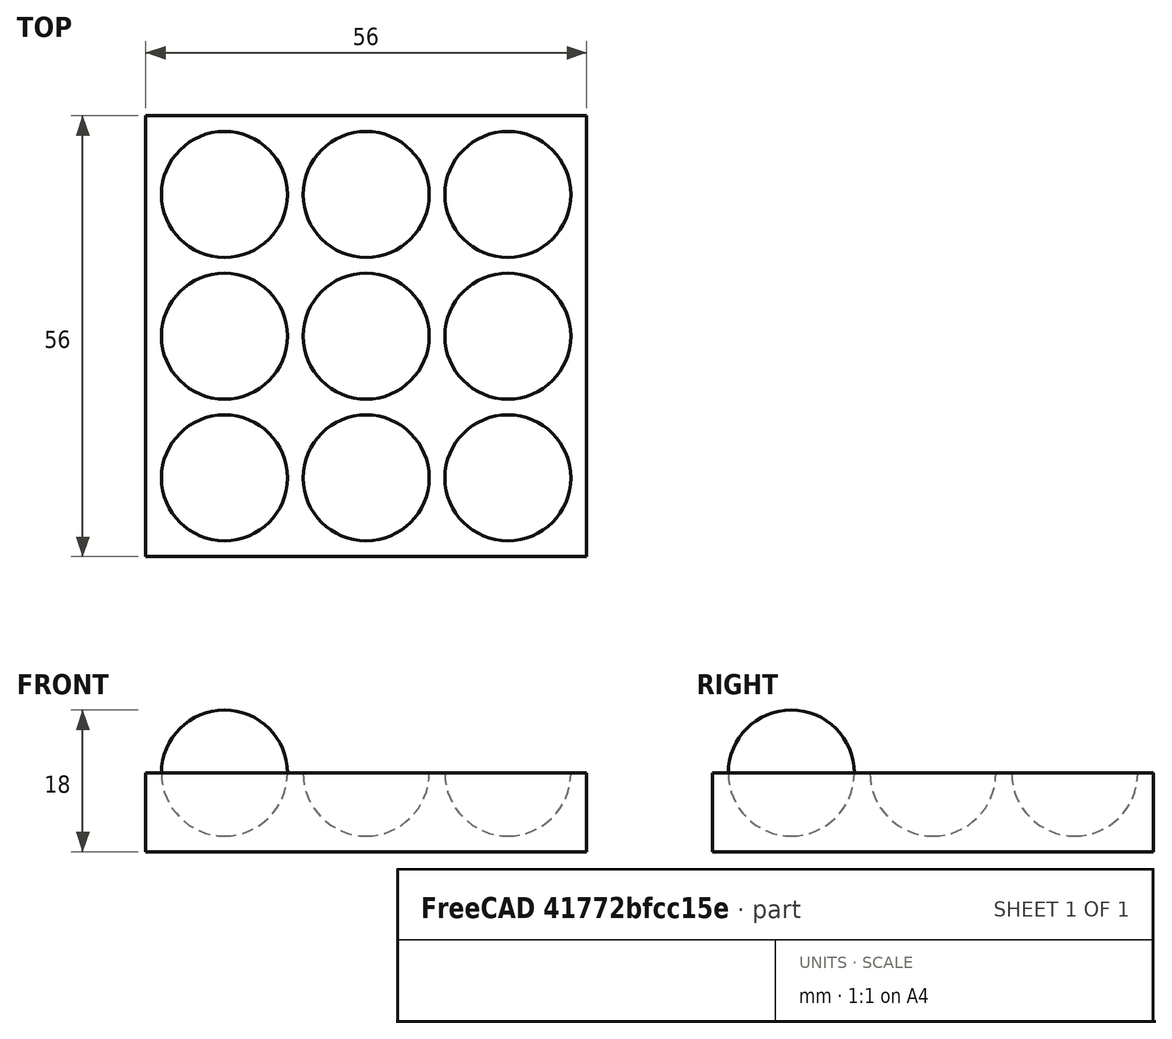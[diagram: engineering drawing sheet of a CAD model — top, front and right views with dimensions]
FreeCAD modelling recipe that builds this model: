
FCSTD DOCUMENT  (FreeCAD 0.20R29177 (Git))
Label: Video13
License: All rights reserved
LicenseURL: http://en.wikipedia.org/wiki/All_rights_reserved
objects: Part::Sphere×1, Part::FeaturePython×1, Part::Box×1, Part::Cut×1
note: 3 computed .brp shape members not serialized (recipe doc carries the construction recipe); baked Part::Feature solids carry a one-line shape summary decoded from their .brp

FEATURE [Part::Sphere] Sphere  label="Esfera"
  Angle1 = -90
  Angle2 = 90
  Angle3 = 360
  AttacherType = Attacher::AttachEngine3D
  Radius = 8
FEATURE [Part::FeaturePython] Array  # Draft array (typed FeaturePython)
  AlwaysSyncPlacement = false
  Angle = 360
  ArrayType = 0
  Axis = (0,0,1)
  Base = -> Sphere
  Center = (0,0,0)
  Count = 9
  ExpandArray = false
  Fuse = false
  IntervalAxis = (0,0,0)
  IntervalX = (18,0,0)
  IntervalY = (0,18,0)
  IntervalZ = (0,0,0)
  NumberCircles = 3
  NumberPolar = 5
  NumberX = 3
  NumberY = 3
  NumberZ = 1
  PlacementList = 9 placements: [(0,0,0),(0,18,0),(0,36,0),(18,0,0),(18,18,0),(18,36,0),(36,0,0),(36,18,0),(36,36,0)]
  RadialDistance = 50
  ScaleList = (9) [(1,1,1),(1,1,1),(1,1,1),(1,1,1),(1,1,1),(1,1,1),(1,1,1),(1,1,1),(1,1,1)]
  Symmetry = 1
  TangentialDistance = 25
FEATURE [Part::Box] Box  label="Cubo"
  AttacherType = Attacher::AttachEngine3D
  Height = 10
  Length = 56
  Placement = pos=(-10,-10,-10) rot=(0,0,1;0rad)
  Width = 56
FEATURE [Part::Cut] Cut
  Base = -> Box
  Tool = -> Array
